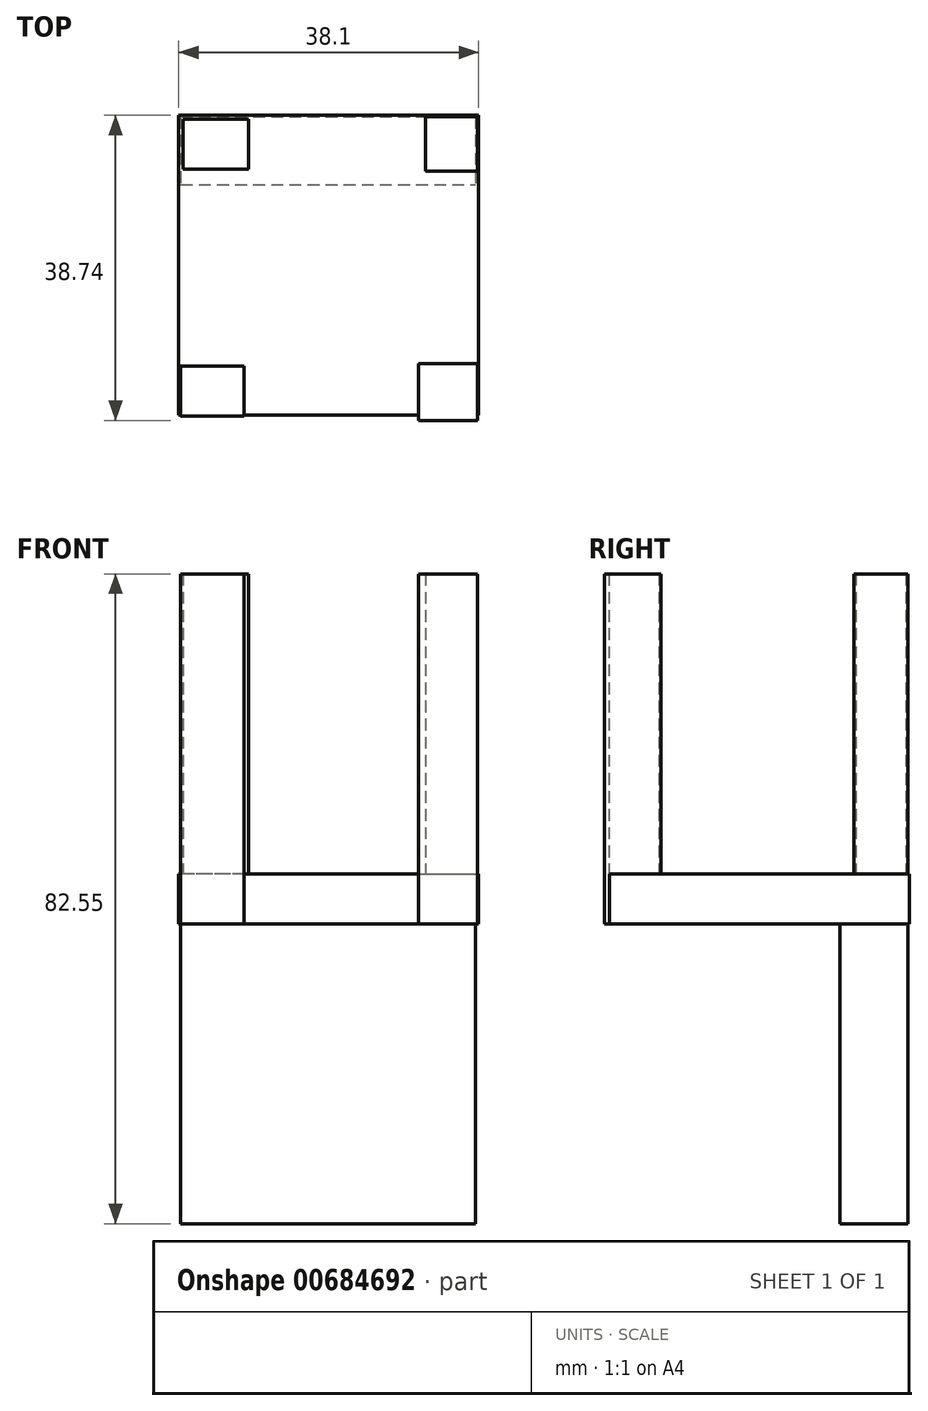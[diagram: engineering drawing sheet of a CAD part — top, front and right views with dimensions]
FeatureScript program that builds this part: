
annotation { "Feature Type Name" : "Feature", "Feature Type Description" : "" }
export const myFeature = defineFeature(function(context is Context, id is Id, definition is map)
    precondition{}
    {
        {
            var Q0;
            Q0=qCreatedBy(makeId("Top.planeOp"),FACE);
            var sketch = newSketch(context, id + "F0", { "sketchPlane" : qUnion([Q0])});
            skLineSegment(sketch, "E0.bottom", {"start": v(-16.82, 19.03) * mm, "end": v(21.28, 19.03) * mm});
            skLineSegment(sketch, "E0.top", {"start": v(-16.82, -19.07) * mm, "end": v(21.28, -19.07) * mm});
            skLineSegment(sketch, "E0.left", {"start": v(-16.82, 19.03) * mm, "end": v(-16.82, -19.07) * mm});
            skLineSegment(sketch, "E0.right", {"start": v(21.28, 19.03) * mm, "end": v(21.28, -19.07) * mm});
            skSolve(sketch);
        }
        {
            var Q0;
            Q0=qSketchRegion(id+"F0",true);
            extrude(context, id + "F1", {"entities" : qUnion([Q0]), "depth" : 6.35 * mm, "offsetDistance" : 25.4 * mm});
        }
        {
            var Q0;
            Q0=qCreatedBy(makeId("Top.planeOp"),FACE);
            var sketch = newSketch(context, id + "F2", { "sketchPlane" : qUnion([Q0])});
            skLineSegment(sketch, "E1.bottom", {"start": v(-16.55, 18.85) * mm, "end": v(20.87, 18.85) * mm});
            skLineSegment(sketch, "E1.top", {"start": v(-16.55, 10.22) * mm, "end": v(20.87, 10.22) * mm});
            skLineSegment(sketch, "E1.left", {"start": v(-16.55, 18.85) * mm, "end": v(-16.55, 10.22) * mm});
            skLineSegment(sketch, "E1.right", {"start": v(20.87, 18.85) * mm, "end": v(20.87, 10.22) * mm});
            skSolve(sketch);
        }
        {
            var Q0;
            Q0=qSketchRegion(id+"F2",true);
            extrude(context, id + "F3", {"entities" : qUnion([Q0]), "operationType" : NewBodyOperationType.ADD, "oppositeDirection" : true, "depth" : 38.1 * mm, "offsetDistance" : 25.4 * mm});
        }
        {
            var Q0;
            Q0=qCreatedBy(makeId("Top.planeOp"),FACE);
            var sketch = newSketch(context, id + "F4", { "sketchPlane" : qUnion([Q0])});
            skLineSegment(sketch, "E2.bottom", {"start": v(-16.55, -19.14) * mm, "end": v(-8.5, -19.14) * mm});
            skLineSegment(sketch, "E2.top", {"start": v(-16.55, -12.8) * mm, "end": v(-8.5, -12.8) * mm});
            skLineSegment(sketch, "E2.left", {"start": v(-16.55, -19.14) * mm, "end": v(-16.55, -12.8) * mm});
            skLineSegment(sketch, "E2.right", {"start": v(-8.5, -19.14) * mm, "end": v(-8.5, -12.8) * mm});
            skLineSegment(sketch, "E3.bottom", {"start": v(21.15, -19.71) * mm, "end": v(13.67, -19.71) * mm});
            skLineSegment(sketch, "E3.top", {"start": v(21.15, -12.52) * mm, "end": v(13.67, -12.52) * mm});
            skLineSegment(sketch, "E3.left", {"start": v(21.15, -19.71) * mm, "end": v(21.15, -12.52) * mm});
            skLineSegment(sketch, "E3.right", {"start": v(13.67, -19.71) * mm, "end": v(13.67, -12.52) * mm});
            skLineSegment(sketch, "E4.bottom", {"start": v(-16.26, 18.56) * mm, "end": v(-7.91, 18.56) * mm});
            skLineSegment(sketch, "E4.top", {"start": v(-16.26, 12.23) * mm, "end": v(-7.91, 12.23) * mm});
            skLineSegment(sketch, "E4.left", {"start": v(-16.26, 18.56) * mm, "end": v(-16.26, 12.23) * mm});
            skLineSegment(sketch, "E4.right", {"start": v(-7.91, 18.56) * mm, "end": v(-7.91, 12.23) * mm});
            skLineSegment(sketch, "E5.bottom", {"start": v(21.15, 18.85) * mm, "end": v(14.53, 18.85) * mm});
            skLineSegment(sketch, "E5.top", {"start": v(21.15, 11.94) * mm, "end": v(14.53, 11.94) * mm});
            skLineSegment(sketch, "E5.left", {"start": v(21.15, 18.85) * mm, "end": v(21.15, 11.94) * mm});
            skLineSegment(sketch, "E5.right", {"start": v(14.53, 18.85) * mm, "end": v(14.53, 11.94) * mm});
            skSolve(sketch);
        }
        {
            var Q0;
            Q0=qSketchRegion(id+"F4",true);
            extrude(context, id + "F5", {"entities" : qUnion([Q0]), "operationType" : NewBodyOperationType.ADD, "depth" : 44.45 * mm, "offsetDistance" : 25.4 * mm});
        }
    });
